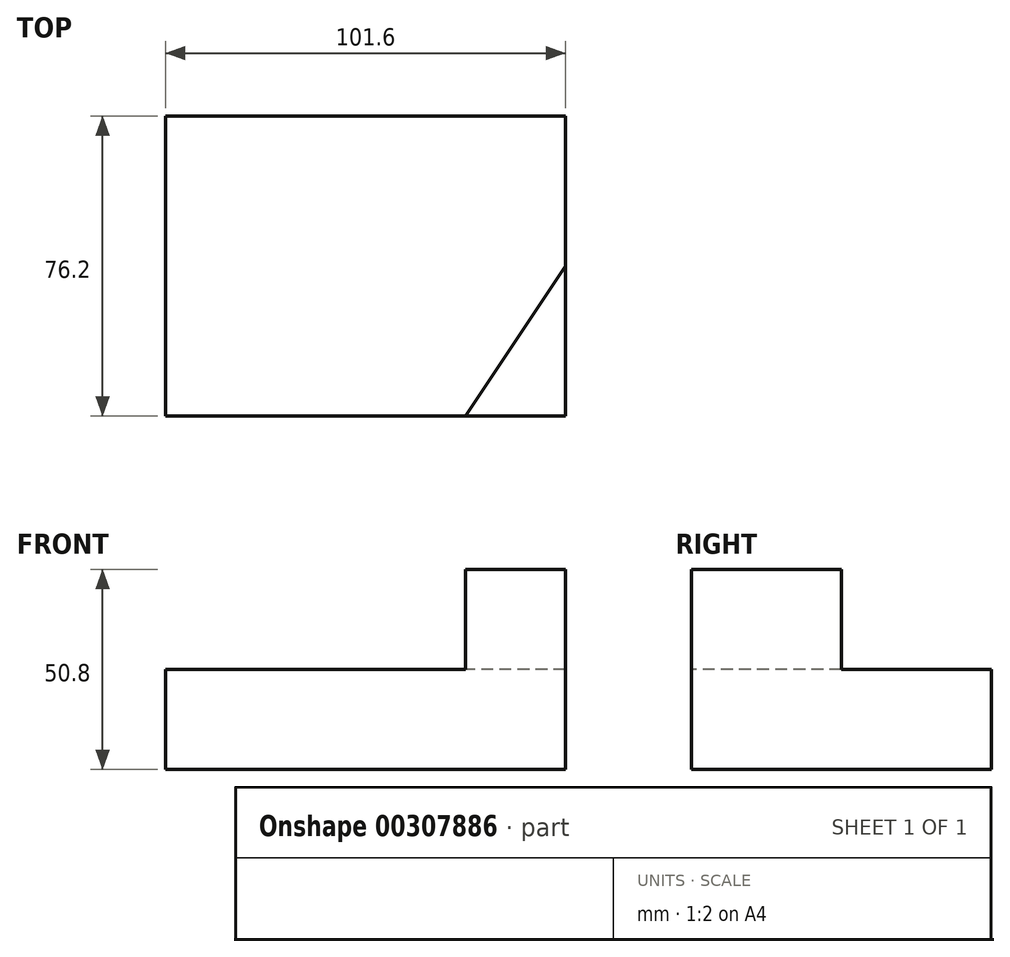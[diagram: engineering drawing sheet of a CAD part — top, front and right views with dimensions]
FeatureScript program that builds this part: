
annotation { "Feature Type Name" : "Feature", "Feature Type Description" : "" }
export const myFeature = defineFeature(function(context is Context, id is Id, definition is map)
    precondition{}
    {
        {
            var Q0;
            Q0=qCreatedBy(makeId("Top.planeOp"),FACE);
            var sketch = newSketch(context, id + "F0", { "sketchPlane" : qUnion([Q0])});
            skLineSegment(sketch, "E0.bottom", {"start": v(-46, 38.45) * mm, "end": v(55.6, 38.45) * mm});
            skLineSegment(sketch, "E0.top", {"start": v(-46, -37.75) * mm, "end": v(55.6, -37.75) * mm});
            skLineSegment(sketch, "E0.left", {"start": v(-46, 38.45) * mm, "end": v(-46, -37.75) * mm});
            skLineSegment(sketch, "E0.right", {"start": v(55.6, 38.45) * mm, "end": v(55.6, -37.75) * mm});
            skSolve(sketch);
        }
        {
            var Q0;
            Q0=makeQuery(id+"F0.imprint","IMPRINT",FACE,{"disambiguationData":[TD([[makeQuery(id+"F0.imprint","IMPRINT",EDGE,{"derivedFrom":sQuery(id+"F0.wireOp",EDGE,"E0.bottom")}),-1.0]])]});
            extrude(context, id + "F1", {"entities" : qUnion([Q0]), "depth" : 25.4 * mm});
        }
        {
            var Q0;
            Q0=makeQuery(id+"F1.opExtrude","CAP_FACE",FACE,{"disambiguationData":[OSD([sQuery(id+"F0.wireOp",EDGE,"E0.bottom"),sQuery(id+"F0.wireOp",EDGE,"E0.top"),sQuery(id+"F0.wireOp",EDGE,"E0.left"),sQuery(id+"F0.wireOp",EDGE,"E0.right")])],"isStart":false});
            var sketch = newSketch(context, id + "F2", { "sketchPlane" : qUnion([Q0])});
            skLineSegment(sketch, "E1", {"start": v(55.6, -37.75) * mm, "end": v(30.2, -37.75) * mm});
            skLineSegment(sketch, "E2", {"start": v(55.6, -37.75) * mm, "end": v(55.6, 0.35) * mm});
            skLineSegment(sketch, "E3", {"start": v(55.6, 0.35) * mm, "end": v(30.2, -37.75) * mm});
            skSolve(sketch);
        }
        {
            var Q0;
            Q0=makeQuery(id+"F2.imprint","IMPRINT",FACE,{"disambiguationData":[TD([[makeQuery(id+"F2.imprint","IMPRINT",EDGE,{"derivedFrom":sQuery(id+"F2.wireOp",EDGE,"E1")}),1.0]])]});
            extrude(context, id + "F3", {"entities" : qUnion([Q0]), "operationType" : NewBodyOperationType.ADD, "depth" : 25.4 * mm});
        }
    });
